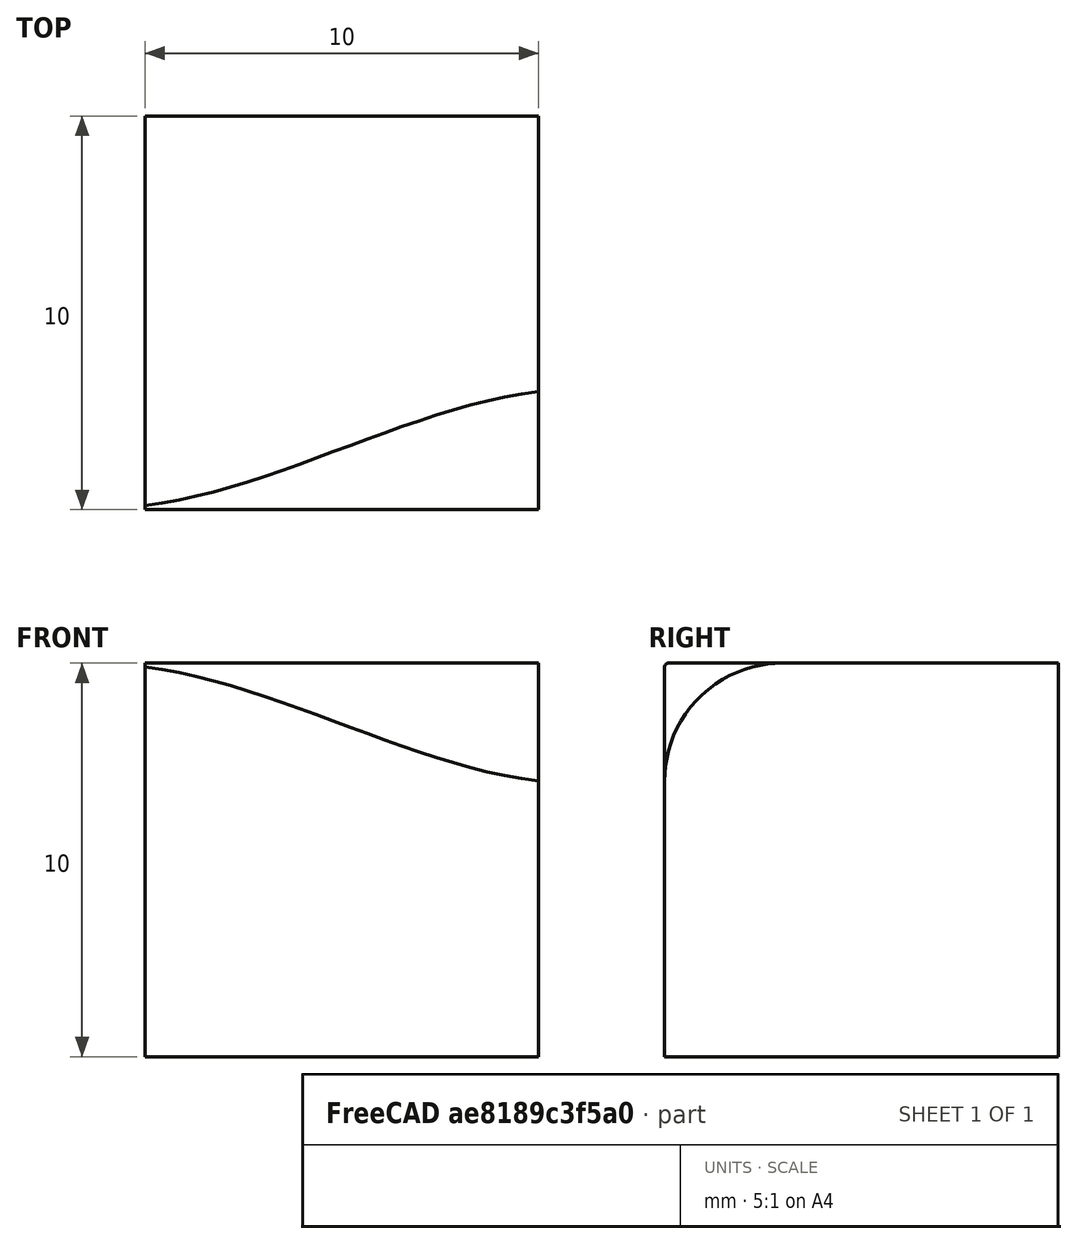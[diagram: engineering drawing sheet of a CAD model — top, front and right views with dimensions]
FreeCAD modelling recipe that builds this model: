
FCSTD DOCUMENT  (FreeCAD 0.19R24267 (Git))
Label: pdwrapper_example_part_workbench_fillet_as_common_additive
License: All rights reserved
LicenseURL: http://en.wikipedia.org/wiki/All_rights_reserved
objects: PartDesign::AdditiveBox×1, Part::Fillet×1, PartDesign::FeatureAdditivePython×1, PartDesign::Body×1
note: 6 computed .brp shape members not serialized (recipe doc carries the construction recipe); baked Part::Feature solids carry a one-line shape summary decoded from their .brp

FEATURE [PartDesign::AdditiveBox] Box
  AttacherType = Attacher::AttachEngine3D
  Height = 10
  Length = 10
  Width = 10
FEATURE [Part::Fillet] Fillet
  Base = -> Box
  Edges = 1 edges: [Edge10 r1=0.1 r2=3]
FEATURE [PartDesign::FeatureAdditivePython] PDW_Common_Add  # link proxy (typed FeaturePython)
  BaseFeature = -> Box
  Body = Body
  ClaimChildren = true
  EditPlacementAdjustments = false
  Enabled = 1
  LinkedObject = -> Fillet
  MeshTolerance = 0.1
  PatternBase = -> Box
  PatternBaseOffset = 0
  PatternBaseScale = 1
  PatternOffsetCut = false
  PatternOffsetJoin = 0
  PatternOffsetMode = 0
  PatternOperation = 3
  PatternOperationDefault = Common
  PatternScaleCut = false
  PatternShapeOffset = 0
  PatternShapeScale = 1
  PatternTool = -> Fillet
  PatternToolOffset = 0
  PatternToolScale = 1
  RefineMesh = true
  ShapeManagement = 0
  ShowMeshProps = false
  ShowOffsetProps = false
  ShowScaleProps = false
  ShowWarnings = true
  TipBase = -> Box
  TipBaseOffset = 0
  TipBaseScale = 1
  TipOffsetCut = false
  TipOffsetJoin = 0
  TipOffsetMode = 0
  TipOperation = 2
  TipOperationDefault = Common
  TipScaleCut = false
  TipShapeOffset = 0
  TipShapeScale = 1
  TipTool = -> Fillet
  TipToolOffset = 0
  TipToolScale = 1
  Type = Additive
  UsePatternBaseAddSubShape = false
  UsePatternToolAddSubShape = false
  UseTipBaseAddSubShape = false
  UseTipToolAddSubShape = false
  Version = 0.2021.10.15
FEATURE [PartDesign::Body] Body
  Group = -> [Box,PDW_Common_Add,Fillet]
  Origin = -> Origin
  Tip = -> PDW_Common_Add
